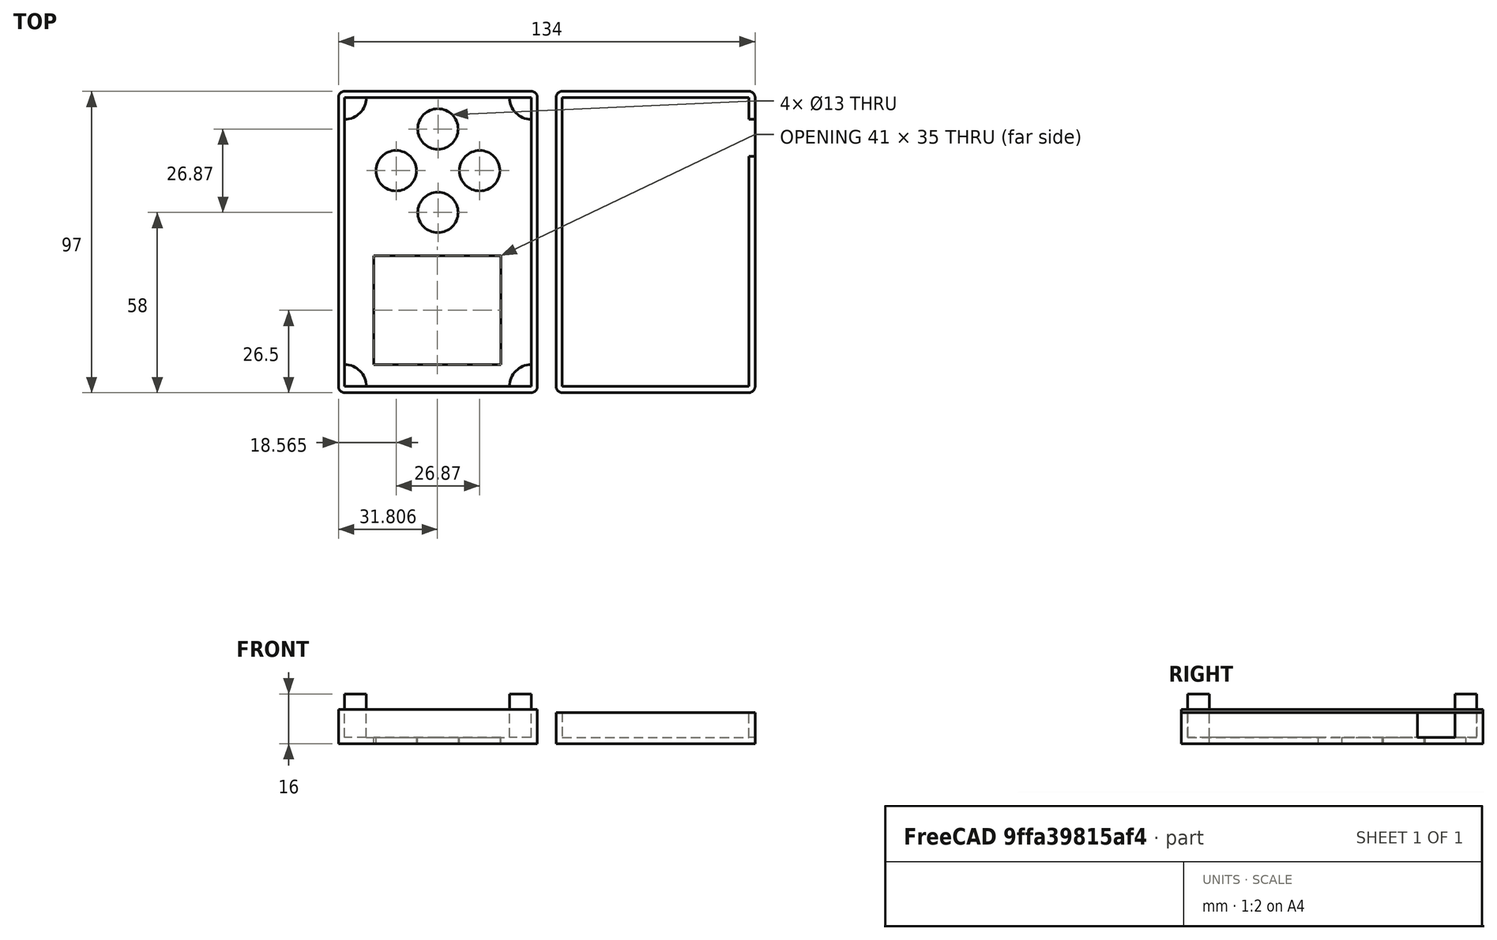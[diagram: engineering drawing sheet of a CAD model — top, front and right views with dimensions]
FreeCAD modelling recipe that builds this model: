
FCSTD DOCUMENT  (FreeCAD 0.18R16131 (Git))
Label: case
License: All rights reserved
LicenseURL: http://en.wikipedia.org/wiki/All_rights_reserved
objects: Sketcher::SketchObject×7, PartDesign::Pocket×4, PartDesign::Pad×3, PartDesign::Body×2, Mesh::Feature×2
note: 23 computed .brp shape members not serialized (recipe doc carries the construction recipe); baked Part::Feature solids carry a one-line shape summary decoded from their .brp

FEATURE [Sketcher::SketchObject] Sketch001
  sketch-geometry (8):
    g0: ArcOfCircle CenterX=0 CenterY=0 CenterZ=0 NormalX=0 NormalY=0 NormalZ=1 AngleXU=0 Radius=2 StartAngle=1.5708 EndAngle=3.14159
    g1: LineSegment StartX=1e-16 StartY=2 StartZ=0 EndX=60 EndY=2 EndZ=0
    g2: ArcOfCircle CenterX=60 CenterY=0 CenterZ=0 NormalX=0 NormalY=0 NormalZ=1 AngleXU=0 Radius=2 StartAngle=0 EndAngle=1.5708
    g3: ArcOfCircle CenterX=0 CenterY=-93 CenterZ=0 NormalX=0 NormalY=0 NormalZ=1 AngleXU=0 Radius=2 StartAngle=3.1416 EndAngle=4.71239
    g4: LineSegment StartX=4.88745e-08 StartY=-95 StartZ=0 EndX=60 EndY=-95 EndZ=0
    g5: ArcOfCircle CenterX=60 CenterY=-93 CenterZ=0 NormalX=0 NormalY=0 NormalZ=1 AngleXU=0 Radius=2 StartAngle=4.71239 EndAngle=6.28319
    g6: LineSegment StartX=-2 StartY=2e-16 StartZ=0 EndX=-2 EndY=-93 EndZ=0
    g7: LineSegment StartX=62 StartY=0 StartZ=0 EndX=62 EndY=-93 EndZ=0
  constraints (27):
    c: Horizontal(g1)
    c: DistanceX(g1,g1) = 60
    c: Coincident(g1,g0)
    c: DistanceX(g0,g0) = 2
    c: DistanceY(g0,g0) = 2
    c: DistanceX(g1,g2) = 2
    c: DistanceY(g2,g1) = 2
    c: Coincident(g2,g1)
    c: Radius(g0) = 2
    c: Radius(g2) = 2
    c: Horizontal(g4)
    c: Coincident(g4,g3)
    c: Coincident(g5,g4)
    c: Radius(g3) = 2
    c: Radius(g5) = 2
    c: Coincident(g0,g-1)
    c: Vertical(g6)
    c: Coincident(g3,g6)
    c: Coincident(g6,g0)
    c: DistanceX(g3,g3) = 2
    c: DistanceY(g3,g3) = 2
    c: DistanceY(g6,g6) = 93
    c: DistanceY(g4,g5) = 2
    c: DistanceX(g5,g5) = 2
    c: Vertical(g7)
    c: Coincident(g5,g7)
    c: Coincident(g7,g2)
FEATURE [PartDesign::Pad] Pad
  Length = 10
  Length2 = 100
  Profile = -> Sketch001
  Type = 0
FEATURE [Sketcher::SketchObject] Sketch  label="Cutout"
  MapMode = 5
  Placement = pos=(0,0,10) rot=(0,0,1;0rad)
  Support = -> [Pad]
  sketch-geometry (4):
    g0: LineSegment StartX=0 StartY=0 StartZ=0 EndX=60 EndY=0 EndZ=0
    g1: LineSegment StartX=60 StartY=0 StartZ=0 EndX=60 EndY=-93 EndZ=0
    g2: LineSegment StartX=60 StartY=-93 StartZ=0 EndX=0 EndY=-93 EndZ=0
    g3: LineSegment StartX=0 StartY=-93 StartZ=0 EndX=0 EndY=0 EndZ=0
  constraints (11):
    c: Coincident(g0,g1)
    c: Coincident(g1,g2)
    c: Coincident(g2,g3)
    c: Coincident(g3,g0)
    c: Horizontal(g0)
    c: Horizontal(g2)
    c: Vertical(g1)
    c: Vertical(g3)
    c: DistanceX(g0,g0) = 60
    c: DistanceY(g3,g3) = 93
    c: Coincident(g0,g-1)
FEATURE [PartDesign::Pocket] Pocket
  BaseFeature = -> Pad
  Length = 8
  Length2 = 100
  Profile = -> Sketch
  Type = 0
FEATURE [Sketcher::SketchObject] Sketch003
  sketch-geometry (8):
    g0: ArcOfCircle CenterX=0 CenterY=0 CenterZ=0 NormalX=0 NormalY=0 NormalZ=1 AngleXU=0 Radius=2 StartAngle=1.5708 EndAngle=3.14159
    g1: LineSegment StartX=1e-16 StartY=2 StartZ=0 EndX=60 EndY=2 EndZ=0
    g2: ArcOfCircle CenterX=60 CenterY=1e-16 CenterZ=0 NormalX=0 NormalY=0 NormalZ=1 AngleXU=0 Radius=2 StartAngle=0 EndAngle=1.5708
    g3: ArcOfCircle CenterX=-1e-16 CenterY=-93 CenterZ=0 NormalX=0 NormalY=0 NormalZ=1 AngleXU=0 Radius=2 StartAngle=3.1416 EndAngle=4.71239
    g4: LineSegment StartX=6.7965e-08 StartY=-95 StartZ=0 EndX=60 EndY=-95 EndZ=0
    g5: ArcOfCircle CenterX=60 CenterY=-93 CenterZ=0 NormalX=0 NormalY=0 NormalZ=1 AngleXU=0 Radius=2 StartAngle=4.71239 EndAngle=6.28319
    g6: LineSegment StartX=-2 StartY=2e-16 StartZ=0 EndX=-2 EndY=-93 EndZ=0
    g7: LineSegment StartX=62 StartY=1e-16 StartZ=0 EndX=62 EndY=-93 EndZ=0
  constraints (27):
    c: Horizontal(g1)
    c: DistanceX(g1,g1) = 60
    c: Coincident(g1,g0)
    c: DistanceX(g0,g0) = 2
    c: DistanceY(g0,g0) = 2
    c: DistanceX(g1,g2) = 2
    c: DistanceY(g2,g1) = 2
    c: Coincident(g2,g1)
    c: Radius(g0) = 2
    c: Radius(g2) = 2
    c: Horizontal(g4)
    c: Coincident(g4,g3)
    c: Coincident(g5,g4)
    c: Radius(g3) = 2
    c: Radius(g5) = 2
    c: Coincident(g0,g-1)
    c: Vertical(g6)
    c: Coincident(g3,g6)
    c: Coincident(g6,g0)
    c: DistanceX(g3,g3) = 2
    c: DistanceY(g3,g3) = 2
    c: DistanceY(g6,g6) = 93
    c: DistanceY(g4,g5) = 2
    c: DistanceX(g5,g5) = 2
    c: Vertical(g7)
    c: Coincident(g5,g7)
    c: Coincident(g7,g2)
FEATURE [PartDesign::Pad] Pad001  label="Body"
  Length = 11
  Length2 = 100
  Profile = -> Sketch003
  Type = 0
FEATURE [Sketcher::SketchObject] Sketch002  label="Cutout001"
  MapMode = 5
  Placement = pos=(0,0,11) rot=(0,0,1;0rad)
  Support = -> [Pad001]
  sketch-geometry (4):
    g0: LineSegment StartX=0 StartY=0 StartZ=0 EndX=60 EndY=0 EndZ=0
    g1: LineSegment StartX=60 StartY=0 StartZ=0 EndX=60 EndY=-93 EndZ=0
    g2: LineSegment StartX=60 StartY=-93 StartZ=0 EndX=0 EndY=-93 EndZ=0
    g3: LineSegment StartX=0 StartY=-93 StartZ=0 EndX=0 EndY=0 EndZ=0
  constraints (11):
    c: Coincident(g0,g1)
    c: Coincident(g1,g2)
    c: Coincident(g2,g3)
    c: Coincident(g3,g0)
    c: Horizontal(g0)
    c: Horizontal(g2)
    c: Vertical(g1)
    c: Vertical(g3)
    c: DistanceX(g0,g0) = 60
    c: DistanceY(g3,g3) = 93
    c: Coincident(g0,g-1)
FEATURE [PartDesign::Pocket] Pocket001  label="Inside"
  BaseFeature = -> Pad001
  Length = 9
  Length2 = 100
  Profile = -> Sketch002
  Type = 0
FEATURE [Sketcher::SketchObject] Sketch004
  MapMode = 5
  Support = -> [XY_Plane003]
  sketch-geometry (21):
    g0: LineSegment StartX=50.6935 StartY=-7 StartZ=0 EndX=50.6935 EndY=-42 EndZ=0
    g1: LineSegment StartX=50.6935 StartY=-42 StartZ=0 EndX=9.69354 EndY=-42 EndZ=0
    g2: LineSegment StartX=9.69354 StartY=-42 StartZ=0 EndX=9.69354 EndY=-7 EndZ=0
    g3: Circle CenterX=30 CenterY=-56 CenterZ=0 NormalX=0 NormalY=0 NormalZ=1 AngleXU=0 Radius=6.5
    g4: Circle CenterX=43.435 CenterY=-69.435 CenterZ=0 NormalX=0 NormalY=0 NormalZ=1 AngleXU=0 Radius=6.5
    g5: Circle CenterX=16.565 CenterY=-69.435 CenterZ=0 NormalX=0 NormalY=0 NormalZ=1 AngleXU=0 Radius=6.5
    g6: Circle CenterX=30 CenterY=-82.8701 CenterZ=0 NormalX=0 NormalY=0 NormalZ=1 AngleXU=0 Radius=6.5
    g7: GeomPoint X=30 Y=-69.435 Z=0
    g8: LineSegment [constr] StartX=43.435 StartY=-69.435 StartZ=0 EndX=16.565 EndY=-69.435 EndZ=0
    g9: LineSegment [constr] StartX=30 StartY=-56 StartZ=0 EndX=30 EndY=-82.8701 EndZ=0
    g10: Circle [constr] CenterX=30 CenterY=-56 CenterZ=0 NormalX=0 NormalY=0 NormalZ=1 AngleXU=0 Radius=9.5
    g11: Circle [constr] CenterX=16.565 CenterY=-69.435 CenterZ=0 NormalX=0 NormalY=0 NormalZ=1 AngleXU=0 Radius=9.5
    g12: Circle [constr] CenterX=43.435 CenterY=-69.435 CenterZ=0 NormalX=0 NormalY=0 NormalZ=1 AngleXU=0 Radius=9.5
    g13: Circle [constr] CenterX=30 CenterY=-82.8701 CenterZ=0 NormalX=0 NormalY=0 NormalZ=1 AngleXU=0 Radius=9.5
    g14: GeomPoint X=0 Y=0 Z=0
    g15: GeomPoint X=60 Y=0 Z=0
    g16: LineSegment [constr] StartX=0 StartY=0 StartZ=0 EndX=30 EndY=0 EndZ=0
    g17: LineSegment [constr] StartX=30 StartY=0 StartZ=0 EndX=60 EndY=0 EndZ=0
    g18: LineSegment [constr] StartX=30 StartY=0 StartZ=0 EndX=30 EndY=-56 EndZ=0
    g19: LineSegment StartX=9.69354 StartY=-7 StartZ=0 EndX=30.1935 EndY=-7 EndZ=0
    g20: LineSegment StartX=30.1935 StartY=-7 StartZ=0 EndX=50.6935 EndY=-7 EndZ=0
  constraints (48):
    c: Coincident(g0,g1)
    c: Coincident(g1,g2)
    c: Horizontal(g1)
    c: Vertical(g0)
    c: Vertical(g2)
    c: Equal(g3,g4) = 5
    c: Equal(g3,g5) = 5
    c: Equal(g3,g6) = 5
    c: Symmetric(g5,g4,g7)
    c: Symmetric(g3,g6,g7)
    c: Diameter(g3) = 13
    c: Distance(g4,g3) = 19
    c: Distance(g3,g5) = 19
    c: Horizontal(g8)
    c: Coincident(g4,g8)
    c: Coincident(g5,g8)
    c: Coincident(g3,g9)
    c: Coincident(g9,g6)
    c: Equal(g9,g8)
    c: Radius(g10) = 9.5
    c: Coincident(g10,g3)
    c: Equal(g10,g11) = 9.5
    c: Equal(g10,g12) = 9.5
    c: Equal(g10,g13) = 9.5
    c: Coincident(g12,g4)
    c: Coincident(g5,g11)
    c: Coincident(g13,g6)
    c: Coincident(g17,g15)
    c: Coincident(g17,g16)
    c: Coincident(g14,g16)
    c: DistanceX(g14,g15) = 60
    c: Coincident(g-1,g14)
    c: Horizontal(g16)
    c: Horizontal(g17)
    c: Equal(g16,g17)
    c: Vertical(g18)
    c: Coincident(g16,g18)
    c: Coincident(g18,g3)
    c: Horizontal(g20)
    c: Horizontal(g19)
    c: Equal(g20,g19)
    c: Coincident(g20,g0)
    c: Coincident(g19,g2)
    c: Coincident(g20,g19)
    c: DistanceX(g2,g0) = 41
    c: DistanceY(g0,g0) = 35
    c: DistanceY(g2,g14) = 7
    c: DistanceY(g18,g18) = 56
FEATURE [PartDesign::Pocket] Pocket002  label="Screen&Buttons"
  BaseFeature = -> Pocket001
  Length = 5
  Length2 = 100
  Profile = -> Sketch004
  Reversed = true
  Type = 0
FEATURE [Sketcher::SketchObject] Sketch005
  MapMode = 5
  Placement = pos=(62,0,0) rot=(0.57735,0.57735,0.57735;2.0944rad)
  Support = -> [Pocket]
  sketch-geometry (6):
    g0: LineSegment [constr] StartX=0 StartY=0 StartZ=0 EndX=-7 EndY=0 EndZ=0
    g1: LineSegment StartX=-19 StartY=10 StartZ=0 EndX=-7 EndY=10 EndZ=0
    g2: LineSegment StartX=-7 StartY=10 StartZ=0 EndX=-7 EndY=2 EndZ=0
    g3: LineSegment StartX=-7 StartY=2 StartZ=0 EndX=-19 EndY=2 EndZ=0
    g4: LineSegment StartX=-19 StartY=2 StartZ=0 EndX=-19 EndY=10 EndZ=0
    g5: LineSegment [constr] StartX=-7 StartY=2 StartZ=0 EndX=-7 EndY=0 EndZ=0
  constraints (17):
    c: Horizontal(g0)
    c: DistanceX(g0,g0) = 7
    c: Coincident(g0,g-1)
    c: Coincident(g1,g2)
    c: Coincident(g2,g3)
    c: Coincident(g3,g4)
    c: Coincident(g4,g1)
    c: Horizontal(g1)
    c: Horizontal(g3)
    c: Vertical(g2)
    c: Vertical(g4)
    c: DistanceX(g1,g1) = 12
    c: DistanceY(g2,g2) = 8
    c: Vertical(g5)
    c: DistanceY(g5,g5) = 2
    c: Coincident(g2,g5)
    c: Coincident(g5,g0)
FEATURE [PartDesign::Pocket] Pocket003
  BaseFeature = -> Pocket
  Length = 2
  Length2 = 100
  Profile = -> Sketch005
  Type = 0
FEATURE [PartDesign::Body] Body002  label="Bottom"
  Group = -> [Sketch001,Pad,Sketch,Pocket,Sketch005,Pocket003]
  Origin = -> Origin002
  Tip = -> Pocket003
FEATURE [Sketcher::SketchObject] Sketch006  label="Stands"
  MapMode = 5
  Placement = pos=(0,0,2) rot=(0,0,1;0rad)
  Support = -> [Pocket002]
  sketch-geometry (16):
    g0: LineSegment [constr] StartX=0 StartY=0 StartZ=0 EndX=60 EndY=0 EndZ=0
    g1: LineSegment [constr] StartX=60 StartY=0 StartZ=0 EndX=60 EndY=-93 EndZ=0
    g2: LineSegment [constr] StartX=60 StartY=-93 StartZ=0 EndX=0 EndY=-93 EndZ=0
    g3: LineSegment [constr] StartX=0 StartY=-93 StartZ=0 EndX=0 EndY=0 EndZ=0
    g4: LineSegment StartX=-1.3e-15 StartY=-1.7e-15 StartZ=0 EndX=7 EndY=-1.7e-15 EndZ=0
    g5: LineSegment StartX=-1.3e-15 StartY=-7 StartZ=0 EndX=-1.3e-15 EndY=-1.8e-15 EndZ=0
    g6: ArcOfCircle CenterX=-1.3e-15 CenterY=-1.7e-15 CenterZ=0 NormalX=0 NormalY=0 NormalZ=1 AngleXU=0 Radius=7 StartAngle=4.71239 EndAngle=6.28319
    g7: LineSegment StartX=60 StartY=0 StartZ=0 EndX=53 EndY=0 EndZ=0
    g8: LineSegment StartX=60 StartY=0 StartZ=0 EndX=60 EndY=-7 EndZ=0
    g9: ArcOfCircle CenterX=60 CenterY=0 CenterZ=0 NormalX=0 NormalY=0 NormalZ=1 AngleXU=0 Radius=7 StartAngle=3.14159 EndAngle=4.71239
    g10: LineSegment StartX=0 StartY=-93 StartZ=0 EndX=0 EndY=-86 EndZ=0
    g11: LineSegment StartX=0 StartY=-93 StartZ=0 EndX=7 EndY=-93 EndZ=0
    g12: ArcOfCircle CenterX=0 CenterY=-93 CenterZ=0 NormalX=0 NormalY=0 NormalZ=1 AngleXU=0 Radius=7 StartAngle=4e-16 EndAngle=1.5708
    g13: LineSegment StartX=60 StartY=-93 StartZ=0 EndX=60 EndY=-86 EndZ=0
    g14: LineSegment StartX=60 StartY=-93 StartZ=0 EndX=53 EndY=-93 EndZ=0
    g15: ArcOfCircle CenterX=60 CenterY=-93 CenterZ=0 NormalX=0 NormalY=0 NormalZ=1 AngleXU=0 Radius=7 StartAngle=1.5708 EndAngle=3.14159
  constraints (43):
    c: Coincident(g3,g0)
    c: Horizontal(g0)
    c: Horizontal(g2)
    c: Vertical(g1)
    c: Vertical(g3)
    c: DistanceX(g0,g0) = 60
    c: DistanceY(g3,g3) = 93
    c: Coincident(g0,g-1)
    c: Coincident(g5,g4)
    c: Horizontal(g4)
    c: Vertical(g5)
    c: DistanceX(g4,g4) = 7
    c: Coincident(g4,g-1)
    c: Coincident(g4,g6)
    c: Coincident(g5,g6)
    c: Coincident(g6,g4)
    c: Horizontal(g7)
    c: Vertical(g8)
    c: Coincident(g9,g0)
    c: Coincident(g9,g7)
    c: Coincident(g9,g8)
    c: Coincident(g7,g9)
    c: Coincident(g8,g7)
    c: Vertical(g10)
    c: Horizontal(g11)
    c: Coincident(g12,g10)
    c: Coincident(g12,g11)
    c: Coincident(g11,g2)
    c: Coincident(g10,g3)
    c: Coincident(g12,g10)
    c: Coincident(g11,g10)
    c: Coincident(g13,g1)
    c: Coincident(g14,g2)
    c: Coincident(g13,g14)
    c: Coincident(g15,g13)
    c: Coincident(g13,g15)
    c: Coincident(g15,g14)
    c: Horizontal(g14)
    c: Vertical(g13)
    c: Coincident(g1,g7)
    c: Equal(g4,g7)
    c: Equal(g11,g4)
    c: Equal(g14,g4)
FEATURE [PartDesign::Pad] Pad002
  BaseFeature = -> Pocket002
  Length = 14
  Length2 = 100
  Profile = -> Sketch006
  Type = 0
FEATURE [PartDesign::Body] Body003  label="Top"
  Group = -> [Sketch003,Pad001,Sketch002,Pocket001,Sketch004,Pocket002,Sketch006,Pad002]
  Origin = -> Origin003
  Placement = pos=(-10,-93,0) rot=(0,0,1;3.14159rad)
  Tip = -> Pad002
FEATURE [Mesh::Feature] Mesh  label="Top (Meshed)"
FEATURE [Mesh::Feature] Mesh001  label="Bottom (Meshed)"
